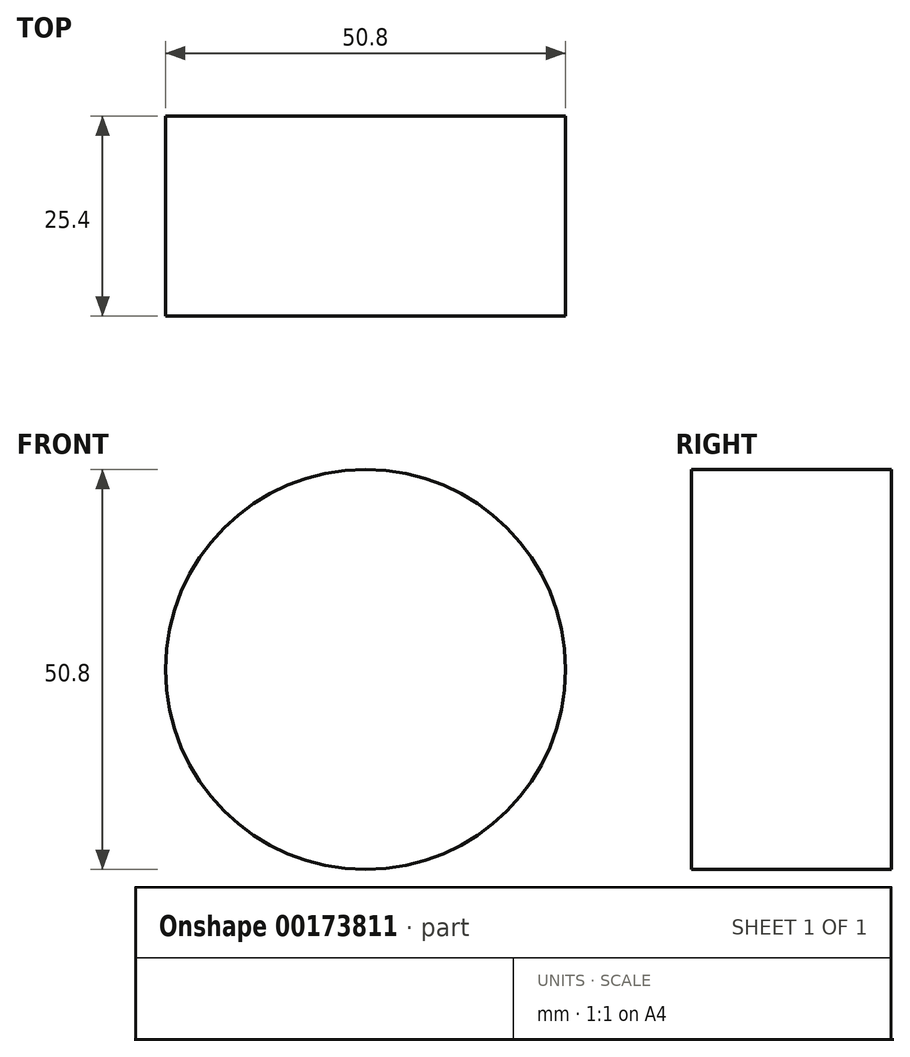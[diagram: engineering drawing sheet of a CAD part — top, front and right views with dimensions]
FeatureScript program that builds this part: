
annotation { "Feature Type Name" : "Feature", "Feature Type Description" : "" }
export const myFeature = defineFeature(function(context is Context, id is Id, definition is map)
    precondition{}
    {
        {
            var Q0;
            Q0=qCreatedBy(makeId("Front.planeOp"),FACE);
            var sketch = newSketch(context, id + "F0", { "sketchPlane" : qUnion([Q0])});
            skCircle(sketch, "E0", {"center": v(0, 0) * mm, "radius": 25.4 * mm});
            skSolve(sketch);
        }
        {
            var Q0;
            Q0=makeQuery(id+"F0.imprint","IMPRINT",FACE,{"disambiguationData":[TD([[makeQuery(id+"F0.imprint","IMPRINT",EDGE,{"derivedFrom":sQuery(id+"F0.wireOp",EDGE,"E0")}),1.0]])]});
            extrude(context, id + "F1", {"entities" : qUnion([Q0]), "oppositeDirection" : true, "depth" : 25.4 * mm});
        }
    });
